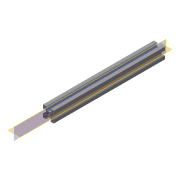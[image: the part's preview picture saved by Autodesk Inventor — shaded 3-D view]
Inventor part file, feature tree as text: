
AUTODESK INVENTOR PART (.ipt)
format: ipt  version: 2019.4 (Build 234330000, 330)  size: 174,592 bytes
history: native  units: mm
features: plane x2, other x2, extrude x1, sketch x1, reference x1
ambient origin geometry x8: Origin, YZ Plane, XZ Plane, XY Plane, X Axis, Y Axis, Z Axis, Center Point
bodies: Solid1 (feature_tree)
feature tree (7):
  extrude  "Extrusion1"  [1 undecoded]
  plane  "Work Plane1"
  plane  "Work Plane2"
  sketch  "Sketch1"  dims[d0=250.0mm d1=0.0mm]
  reference  "Reference1"
  other  "Assembly_neje_slide_y_wellplateholder_20mmrod.iam"
  other  "00_V-Slot_20x:1"
note: 1 required parameter value undecoded (feature->parameter linkage not recoverable at this tier; creation-order binding heuristic only, values carry confidence <= 0.55)
